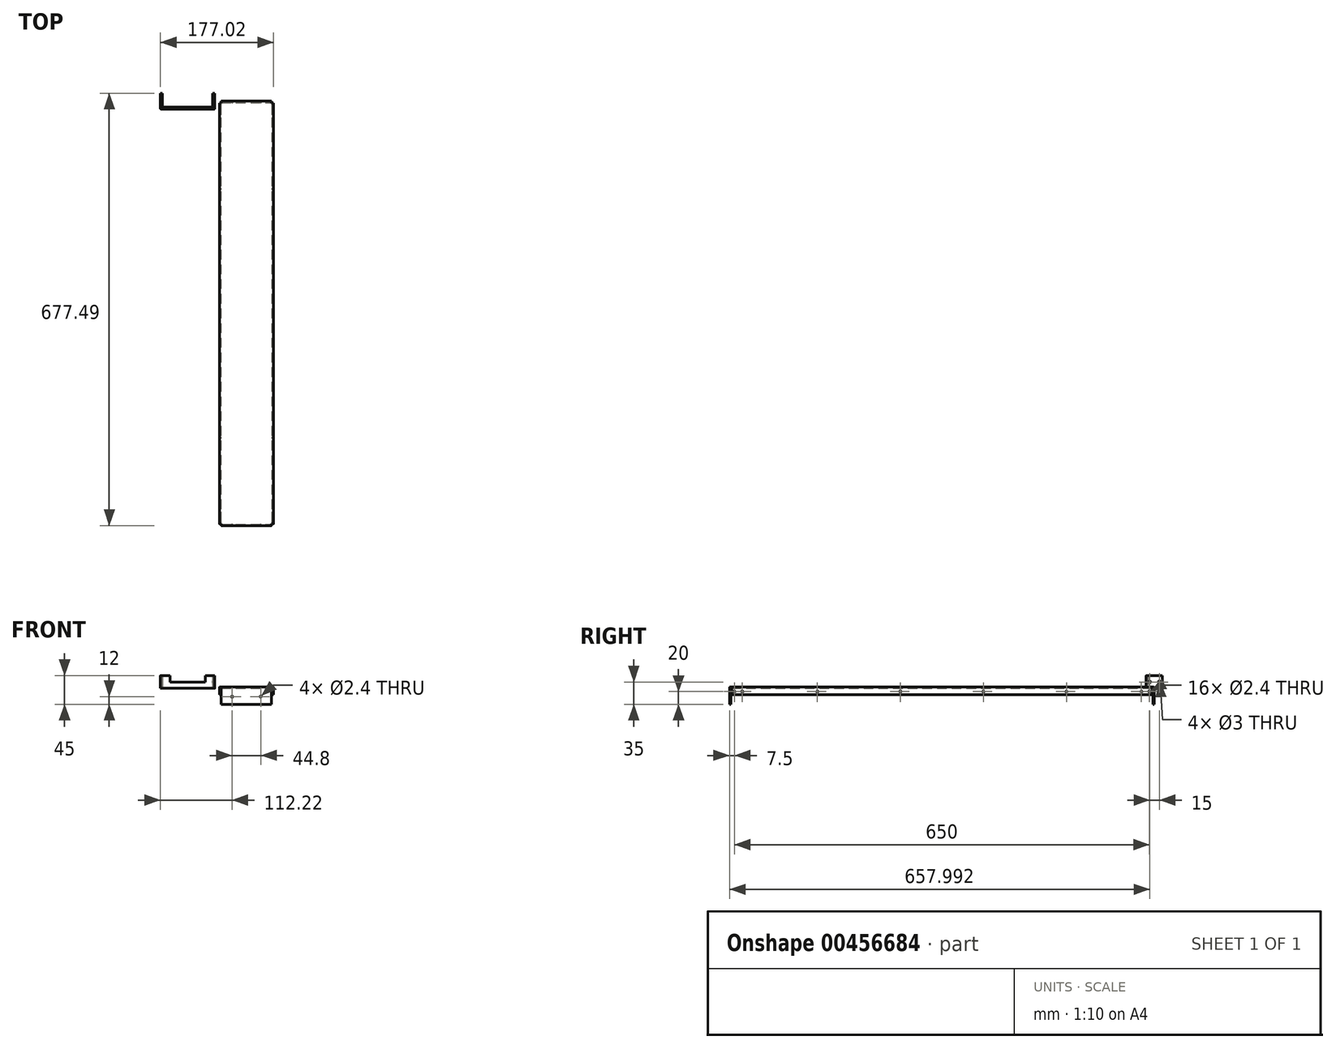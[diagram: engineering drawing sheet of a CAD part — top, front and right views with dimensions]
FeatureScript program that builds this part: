
annotation { "Feature Type Name" : "Feature", "Feature Type Description" : "" }
export const myFeature = defineFeature(function(context is Context, id is Id, definition is map)
    precondition{}
    {
        {
            var Q0;
            Q0=qCreatedBy(makeId("Top.planeOp"),FACE);
            var sketch = newSketch(context, id + "F0", { "sketchPlane" : qUnion([Q0])});
            skLineSegment(sketch, "E0.bottom", {"start": v(42.4, -332.5) * mm, "end": v(-42.4, -332.5) * mm});
            skLineSegment(sketch, "E0.top", {"start": v(42.4, 332.5) * mm, "end": v(-42.4, 332.5) * mm});
            skLineSegment(sketch, "E0.left", {"start": v(42.4, -332.5) * mm, "end": v(42.4, 332.5) * mm});
            skLineSegment(sketch, "E0.right", {"start": v(-42.4, -332.5) * mm, "end": v(-42.4, 332.5) * mm});
            skPoint(sketch, "E0.middle", {"position": v(0, 0) * mm});
            skSolve(sketch);
        }
        {
            var Q0;
            Q0=qSketchRegion(id+"F0",true);
            extrude(context, id + "F1", {"entities" : qUnion([Q0]), "depth" : 2 * mm});
        }
        {
            var Q0;
            Q0=makeQuery(id+"F1.opExtrude","CAP_FACE",FACE,{"disambiguationData":[OSD([sQuery(id+"F0.wireOp",EDGE,"E0.bottom"),sQuery(id+"F0.wireOp",EDGE,"E0.top"),sQuery(id+"F0.wireOp",EDGE,"E0.left"),sQuery(id+"F0.wireOp",EDGE,"E0.right")])],"isStart":false});
            var sketch = newSketch(context, id + "F2", { "sketchPlane" : qUnion([Q0])});
            skLineSegment(sketch, "E1.bottom", {"start": v(-42.4, 332.5) * mm, "end": v(-39.4, 332.5) * mm});
            skLineSegment(sketch, "E1.top", {"start": v(-42.4, 329.5) * mm, "end": v(-39.4, 329.5) * mm});
            skLineSegment(sketch, "E1.left", {"start": v(-42.4, 332.5) * mm, "end": v(-42.4, 329.5) * mm});
            skLineSegment(sketch, "E1.right", {"start": v(-39.4, 332.5) * mm, "end": v(-39.4, 329.5) * mm});
            skLineSegment(sketch, "E2.bottom", {"start": v(42.4, 332.5) * mm, "end": v(39.4, 332.5) * mm});
            skLineSegment(sketch, "E2.top", {"start": v(42.4, 329.5) * mm, "end": v(39.4, 329.5) * mm});
            skLineSegment(sketch, "E2.left", {"start": v(42.4, 332.5) * mm, "end": v(42.4, 329.5) * mm});
            skLineSegment(sketch, "E2.right", {"start": v(39.4, 332.5) * mm, "end": v(39.4, 329.5) * mm});
            skLineSegment(sketch, "E3.bottom", {"start": v(42.4, -332.5) * mm, "end": v(39.4, -332.5) * mm});
            skLineSegment(sketch, "E3.top", {"start": v(42.4, -329.5) * mm, "end": v(39.4, -329.5) * mm});
            skLineSegment(sketch, "E3.left", {"start": v(42.4, -332.5) * mm, "end": v(42.4, -329.5) * mm});
            skLineSegment(sketch, "E3.right", {"start": v(39.4, -332.5) * mm, "end": v(39.4, -329.5) * mm});
            skLineSegment(sketch, "E4.bottom", {"start": v(-42.4, -332.5) * mm, "end": v(-39.4, -332.5) * mm});
            skLineSegment(sketch, "E4.top", {"start": v(-42.4, -329.5) * mm, "end": v(-39.4, -329.5) * mm});
            skLineSegment(sketch, "E4.left", {"start": v(-42.4, -332.5) * mm, "end": v(-42.4, -329.5) * mm});
            skLineSegment(sketch, "E4.right", {"start": v(-39.4, -332.5) * mm, "end": v(-39.4, -329.5) * mm});
            skSolve(sketch);
        }
        {
            var Q0;
            Q0=qSketchRegion(id+"F2",true);
            extrude(context, id + "F3", {"entities" : qUnion([Q0]), "operationType" : NewBodyOperationType.REMOVE, "oppositeDirection" : true, "depth" : 2 * mm});
        }
        {
            var Q0;
            Q0=makeQuery(id+"F1.opExtrude","CAP_FACE",FACE,{"disambiguationData":[OSD([sQuery(id+"F0.wireOp",EDGE,"E0.bottom"),sQuery(id+"F0.wireOp",EDGE,"E0.top"),sQuery(id+"F0.wireOp",EDGE,"E0.left"),sQuery(id+"F0.wireOp",EDGE,"E0.right")])],"isStart":true});
            var sketch = newSketch(context, id + "F4", { "sketchPlane" : qUnion([Q0])});
            skLineSegment(sketch, "E5.bottom", {"start": v(-39.4, -332.5) * mm, "end": v(39.4, -332.5) * mm});
            skLineSegment(sketch, "E5.top", {"start": v(-39.4, -330.5) * mm, "end": v(39.4, -330.5) * mm});
            skLineSegment(sketch, "E5.left", {"start": v(-39.4, -330.5) * mm, "end": v(-39.4, -332.5) * mm});
            skLineSegment(sketch, "E5.right", {"start": v(39.4, -330.5) * mm, "end": v(39.4, -332.5) * mm});
            skLineSegment(sketch, "E6.bottom", {"start": v(-42.4, -329.5) * mm, "end": v(-40.4, -329.5) * mm});
            skLineSegment(sketch, "E6.top", {"start": v(-42.4, 329.5) * mm, "end": v(-40.4, 329.5) * mm});
            skLineSegment(sketch, "E6.left", {"start": v(-42.4, -329.5) * mm, "end": v(-42.4, 329.5) * mm});
            skLineSegment(sketch, "E6.right", {"start": v(-40.4, -329.5) * mm, "end": v(-40.4, 329.5) * mm});
            skLineSegment(sketch, "E7.bottom", {"start": v(-39.4, 332.5) * mm, "end": v(39.4, 332.5) * mm});
            skLineSegment(sketch, "E7.top", {"start": v(-39.4, 330.5) * mm, "end": v(39.4, 330.5) * mm});
            skLineSegment(sketch, "E7.left", {"start": v(-39.4, 332.5) * mm, "end": v(-39.4, 330.5) * mm});
            skLineSegment(sketch, "E7.right", {"start": v(39.4, 332.5) * mm, "end": v(39.4, 330.5) * mm});
            skLineSegment(sketch, "E8.bottom", {"start": v(42.4, 329.5) * mm, "end": v(40.4, 329.5) * mm});
            skLineSegment(sketch, "E8.top", {"start": v(42.4, -329.5) * mm, "end": v(40.4, -329.5) * mm});
            skLineSegment(sketch, "E8.left", {"start": v(42.4, 329.5) * mm, "end": v(42.4, -329.5) * mm});
            skLineSegment(sketch, "E8.right", {"start": v(40.4, 329.5) * mm, "end": v(40.4, -329.5) * mm});
            skSolve(sketch);
        }
        {
            var Q0;
            Q0=makeQuery(id+"F4.imprint","IMPRINT",FACE,{"disambiguationData":[TD([[makeQuery(id+"F4.imprint","IMPRINT",EDGE,{"derivedFrom":sQuery(id+"F4.wireOp",EDGE,"E7.bottom")}),1.0]])]});
            var Q1;
            Q1=makeQuery(id+"F4.imprint","IMPRINT",FACE,{"disambiguationData":[TD([[makeQuery(id+"F4.imprint","IMPRINT",EDGE,{"derivedFrom":sQuery(id+"F4.wireOp",EDGE,"E5.bottom")}),-1.0]])]});
            extrude(context, id + "F5", {"entities" : qUnion([Q0, Q1]), "operationType" : NewBodyOperationType.ADD, "depth" : 25 * mm});
        }
        {
            var Q0;
            Q0=makeQuery(id+"F4.imprint","IMPRINT",FACE,{"disambiguationData":[TD([[makeQuery(id+"F4.imprint","IMPRINT",EDGE,{"derivedFrom":sQuery(id+"F4.wireOp",EDGE,"E6.bottom")}),1.0]])]});
            var Q1;
            Q1=makeQuery(id+"F4.imprint","IMPRINT",FACE,{"disambiguationData":[TD([[makeQuery(id+"F4.imprint","IMPRINT",EDGE,{"derivedFrom":sQuery(id+"F4.wireOp",EDGE,"E8.bottom")}),1.0]])]});
            extrude(context, id + "F6", {"entities" : qUnion([Q0, Q1]), "operationType" : NewBodyOperationType.ADD, "depth" : 10 * mm});
        }
        {
            var Q0;
            Q0=makeQuery(id+"F1.opExtrude","CAP_EDGE",EDGE,{"disambiguationData":[OSD([sQuery(id+"F0.wireOp",EDGE,"E0.top")])],"isStart":false});
            var Q1;
            Q1=makeQuery(id+"F1.opExtrude","CAP_EDGE",EDGE,{"disambiguationData":[OSD([sQuery(id+"F0.wireOp",EDGE,"E0.right")])],"isStart":false});
            var Q2;
            Q2=makeQuery(id+"F5.opExtrude","CAP_EDGE",EDGE,{"disambiguationData":[OSD([sQuery(id+"F4.wireOp",EDGE,"E5.top")])],"isStart":true});
            var Q3;
            Q3=makeQuery(id+"F5.opExtrude","CAP_EDGE",EDGE,{"disambiguationData":[OSD([sQuery(id+"F4.wireOp",EDGE,"E6.right")])],"isStart":true});
            var Q4;
            Q4=makeQuery(id+"F5.opExtrude","CAP_EDGE",EDGE,{"disambiguationData":[OSD([sQuery(id+"F4.wireOp",EDGE,"E8.right")])],"isStart":true});
            var Q5;
            Q5=makeQuery(id+"F1.opExtrude","CAP_EDGE",EDGE,{"disambiguationData":[OSD([sQuery(id+"F0.wireOp",EDGE,"E0.left")])],"isStart":false});
            var Q6;
            Q6=makeQuery(id+"F1.opExtrude","CAP_EDGE",EDGE,{"disambiguationData":[OSD([sQuery(id+"F0.wireOp",EDGE,"E0.bottom")])],"isStart":false});
            var Q7;
            Q7=makeQuery(id+"F5.opExtrude","CAP_EDGE",EDGE,{"disambiguationData":[OSD([sQuery(id+"F4.wireOp",EDGE,"E7.top")])],"isStart":true});
            fillet(context, id + "F7", {"entities" : qUnion([Q0, Q1, Q2, Q3, Q4, Q5, Q6, Q7]), "radius" : 1 * mm, "tangentPropagation" : true, "allowEdgeOverflow" : false});
        }
        {
            var Q0;
            Q0=makeQuery(id+"F5.boolean.opBoolean","MERGE",FACE,{"derivedFrom":[makeQuery(id+"F1.opExtrude","SWEPT_FACE",FACE,{"disambiguationData":[OSD([sQuery(id+"F0.wireOp",EDGE,"E0.top")])]}),makeQuery(id+"F5.opExtrude","SWEPT_FACE",FACE,{"disambiguationData":[OSD([sQuery(id+"F4.wireOp",EDGE,"E5.bottom")])]})]});
            var sketch = newSketch(context, id + "F8", { "sketchPlane" : qUnion([Q0])});
            skCircle(sketch, "E9", {"center": v(-22.4, -13) * mm, "radius": 1.2 * mm});
            skCircle(sketch, "E10", {"center": v(22.4, -13) * mm, "radius": 1.2 * mm});
            skSolve(sketch);
        }
        {
            var Q0;
            Q0=qSketchRegion(id+"F8",true);
            extrude(context, id + "F9", {"entities" : qUnion([Q0]), "operationType" : NewBodyOperationType.REMOVE, "endBound" : BoundingType.THROUGH_ALL, "oppositeDirection" : true, "depth" : 25 * mm});
        }
        {
            var Q0;
            Q0=makeQuery(id+"F6.boolean.opBoolean","MERGE",FACE,{"derivedFrom":[makeQuery(id+"F1.opExtrude","SWEPT_FACE",FACE,{"disambiguationData":[OSD([sQuery(id+"F0.wireOp",EDGE,"E0.left")])]}),makeQuery(id+"F6.opExtrude","SWEPT_FACE",FACE,{"disambiguationData":[OSD([sQuery(id+"F4.wireOp",EDGE,"E8.left")])]})]});
            var sketch = newSketch(context, id + "F10", { "sketchPlane" : qUnion([Q0])});
            skCircle(sketch, "E11", {"center": v(325, -5) * mm, "radius": 1.2 * mm});
            skCircle(sketch, "E12.1.0.0", {"center": v(195, -5) * mm, "radius": 1.2 * mm});
            skCircle(sketch, "E12.2.0.0", {"center": v(65, -5) * mm, "radius": 1.2 * mm});
            skCircle(sketch, "E12.3.0.0", {"center": v(-65, -5) * mm, "radius": 1.2 * mm});
            skCircle(sketch, "E12.4.0.0", {"center": v(-195, -5) * mm, "radius": 1.2 * mm});
            skCircle(sketch, "E12.5.0.0", {"center": v(-325, -5) * mm, "radius": 1.2 * mm});
            skLineSegment(sketch, "E12.direction1", {"start": v(325, -5) * mm, "end": v(195, -5) * mm, "construction": true});
            skCircle(sketch, "E13", {"center": v(312.5, -5) * mm, "radius": 1.2 * mm});
            skCircle(sketch, "E14", {"center": v(-312.5, -5) * mm, "radius": 1.2 * mm});
            skSolve(sketch);
        }
        {
            var Q0;
            Q0=qSketchRegion(id+"F10",true);
            extrude(context, id + "F11", {"entities" : qUnion([Q0]), "operationType" : NewBodyOperationType.REMOVE, "endBound" : BoundingType.THROUGH_ALL, "oppositeDirection" : true, "depth" : 25 * mm});
        }
        {
            var Q0;
            Q0=qCreatedBy(makeId("Top.planeOp"),FACE);
            var sketch = newSketch(context, id + "F12", { "sketchPlane" : qUnion([Q0])});
            skLineSegment(sketch, "E15.bottom", {"start": v(-131.62, 323) * mm, "end": v(-52.62, 323) * mm});
            skLineSegment(sketch, "E15.top", {"start": v(-131.62, 320) * mm, "end": v(-52.62, 320) * mm});
            skLineSegment(sketch, "E15.left", {"start": v(-131.62, 323) * mm, "end": v(-131.62, 320) * mm});
            skLineSegment(sketch, "E15.right", {"start": v(-52.62, 323) * mm, "end": v(-52.62, 320) * mm});
            skLineSegment(sketch, "E16.bottom", {"start": v(-131.62, 320) * mm, "end": v(-134.62, 320) * mm});
            skLineSegment(sketch, "E16.top", {"start": v(-131.62, 345) * mm, "end": v(-134.62, 345) * mm});
            skLineSegment(sketch, "E16.left", {"start": v(-131.62, 320) * mm, "end": v(-131.62, 345) * mm});
            skLineSegment(sketch, "E16.right", {"start": v(-134.62, 320) * mm, "end": v(-134.62, 345) * mm});
            skLineSegment(sketch, "E17.bottom", {"start": v(-52.62, 320) * mm, "end": v(-49.62, 320) * mm});
            skLineSegment(sketch, "E17.top", {"start": v(-52.62, 345) * mm, "end": v(-49.62, 345) * mm});
            skLineSegment(sketch, "E17.left", {"start": v(-52.62, 320) * mm, "end": v(-52.62, 345) * mm});
            skLineSegment(sketch, "E17.right", {"start": v(-49.62, 320) * mm, "end": v(-49.62, 345) * mm});
            skSolve(sketch);
        }
        {
            var Q0;
            Q0=qSketchRegion(id+"F12",true);
            extrude(context, id + "F13", {"entities" : qUnion([Q0]), "depth" : 20 * mm});
        }
        {
            var Q0;
            Q0=makeQuery(id+"F13.opExtrude","SWEPT_FACE",FACE,{"disambiguationData":[OSD([sQuery(id+"F12.wireOp",EDGE,"E16.right")])]});
            var sketch = newSketch(context, id + "F14", { "sketchPlane" : qUnion([Q0])});
            skCircle(sketch, "E18", {"center": v(-325.5, 10) * mm, "radius": 1.5 * mm});
            skCircle(sketch, "E19", {"center": v(-340.5, 10) * mm, "radius": 1.5 * mm});
            skSolve(sketch);
        }
        {
            var Q0;
            Q0=qSketchRegion(id+"F14",true);
            extrude(context, id + "F15", {"entities" : qUnion([Q0]), "operationType" : NewBodyOperationType.REMOVE, "endBound" : BoundingType.THROUGH_ALL, "oppositeDirection" : true, "depth" : 25 * mm});
        }
        {
            var Q0;
            Q0=makeQuery(id+"F13.opExtrude","SWEPT_EDGE",EDGE,{"disambiguationData":[OSD([sQuery(id+"F12.wireOp",EDGE,"E17.bottom"),sQuery(id+"F12.wireOp",EDGE,"E17.right")])]});
            var Q1;
            Q1=makeQuery(id+"F13.opExtrude","SWEPT_EDGE",EDGE,{"disambiguationData":[OSD([sQuery(id+"F12.wireOp",EDGE,"E15.bottom"),sQuery(id+"F12.wireOp",EDGE,"E17.left")])]});
            var Q2;
            Q2=makeQuery(id+"F13.opExtrude","SWEPT_EDGE",EDGE,{"disambiguationData":[OSD([sQuery(id+"F12.wireOp",EDGE,"E16.bottom"),sQuery(id+"F12.wireOp",EDGE,"E16.right")])]});
            var Q3;
            Q3=makeQuery(id+"F13.opExtrude","SWEPT_EDGE",EDGE,{"disambiguationData":[OSD([sQuery(id+"F12.wireOp",EDGE,"E15.bottom"),sQuery(id+"F12.wireOp",EDGE,"E16.left")])]});
            fillet(context, id + "F16", {"entities" : qUnion([Q0, Q1, Q2, Q3]), "radius" : 1 * mm, "tangentPropagation" : true, "allowEdgeOverflow" : false});
        }
        {
            var Q0;
            Q0=makeQuery(id+"F13.opExtrude","SWEPT_FACE",FACE,{"disambiguationData":[OSD([sQuery(id+"F12.wireOp",EDGE,"E15.top"),sQuery(id+"F12.wireOp",EDGE,"E16.bottom"),sQuery(id+"F12.wireOp",EDGE,"E17.bottom")])]});
            var sketch = newSketch(context, id + "F17", { "sketchPlane" : qUnion([Q0])});
            skLineSegment(sketch, "E20.bottom", {"start": v(-64.62, 10) * mm, "end": v(-119.62, 10) * mm});
            skLineSegment(sketch, "E20.top", {"start": v(-64.62, 20) * mm, "end": v(-119.62, 20) * mm});
            skLineSegment(sketch, "E20.left", {"start": v(-64.62, 10) * mm, "end": v(-64.62, 20) * mm});
            skLineSegment(sketch, "E20.right", {"start": v(-119.62, 10) * mm, "end": v(-119.62, 20) * mm});
            skPoint(sketch, "E20.middle", {"position": v(-92.12, 15) * mm});
            skSolve(sketch);
        }
        {
            var Q0;
            Q0=qSketchRegion(id+"F17",true);
            extrude(context, id + "F18", {"entities" : qUnion([Q0]), "operationType" : NewBodyOperationType.REMOVE, "oppositeDirection" : true, "depth" : 3 * mm});
        }
    });
